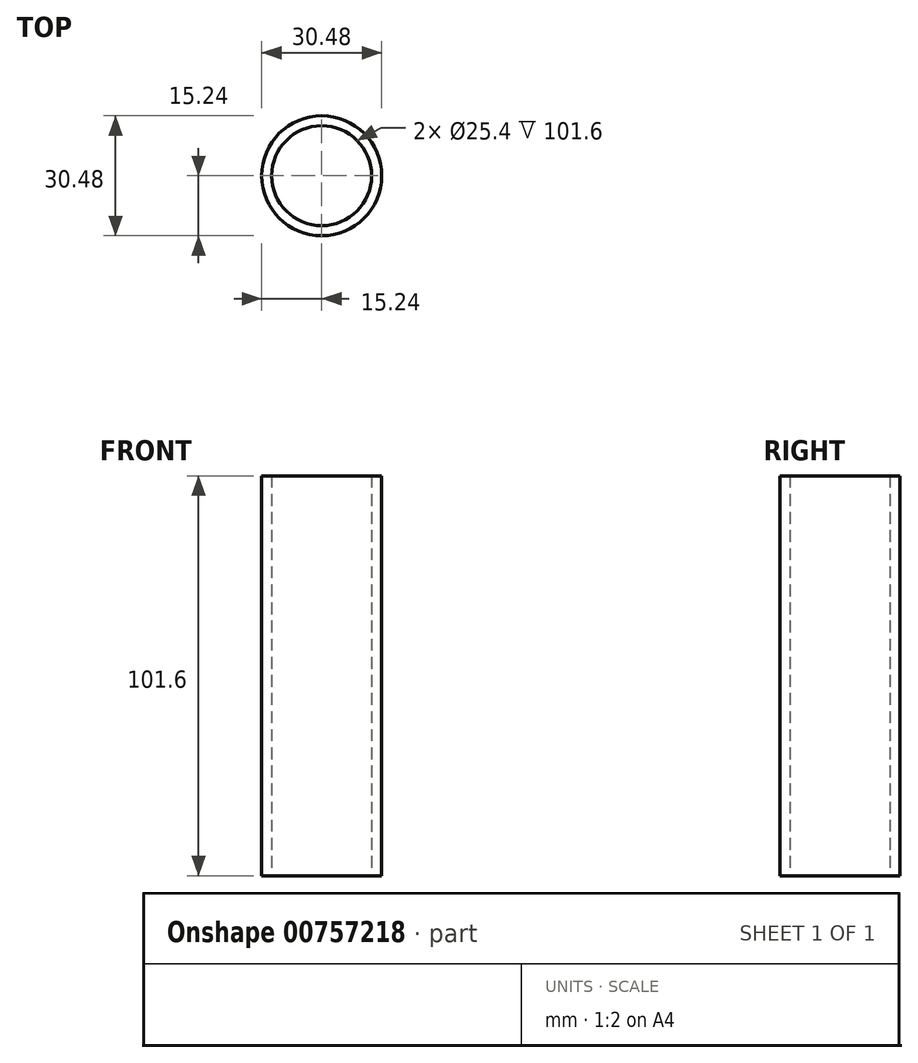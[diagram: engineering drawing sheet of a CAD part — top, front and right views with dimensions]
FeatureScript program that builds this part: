
annotation { "Feature Type Name" : "Feature", "Feature Type Description" : "" }
export const myFeature = defineFeature(function(context is Context, id is Id, definition is map)
    precondition{}
    {
        {
            var Q0;
            Q0=qCreatedBy(makeId("Top.planeOp"),FACE);
            var sketch = newSketch(context, id + "F0", { "sketchPlane" : qUnion([Q0])});
            skCircle(sketch, "E0", {"center": v(0, 0) * mm, "radius": 15.24 * mm});
            skCircle(sketch, "E1", {"center": v(0, 0) * mm, "radius": 12.7 * mm});
            skSolve(sketch);
        }
        {
            var Q0;
            Q0 = qSketchRegion(id + "F0", true);
            extrude(context, id + "F1", {"entities" : qUnion([Q0]), "depth" : 101.6 * mm, "offsetDistance" : 25.4 * mm});
        }
    });
